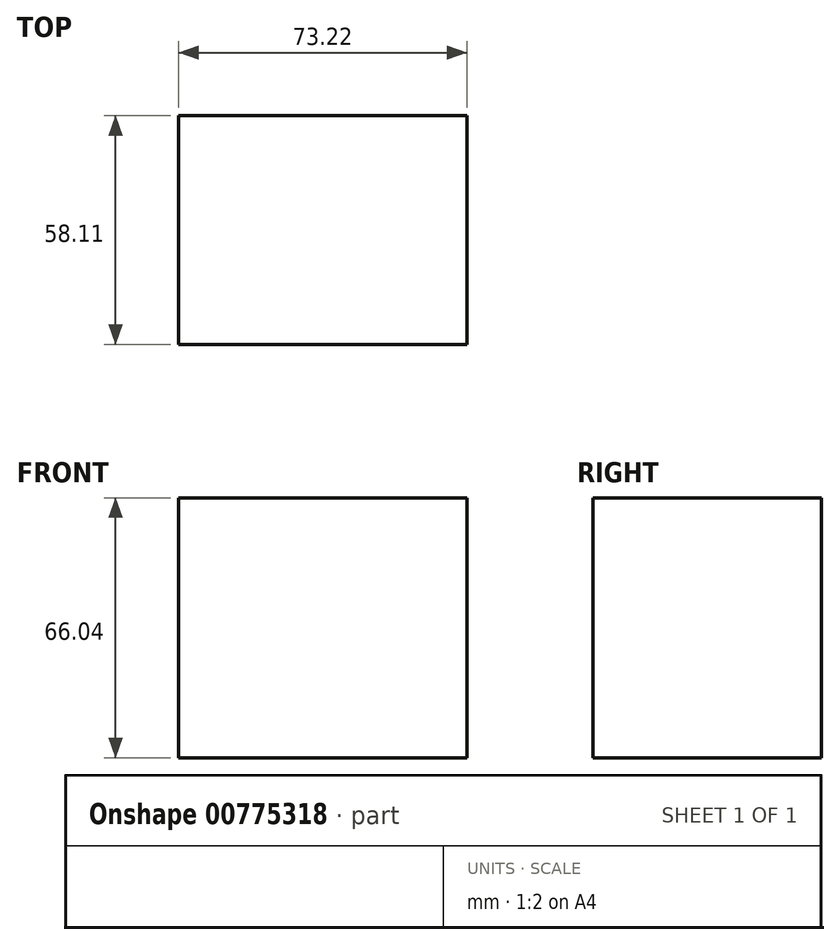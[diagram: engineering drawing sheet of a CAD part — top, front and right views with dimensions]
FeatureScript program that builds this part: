
annotation { "Feature Type Name" : "Feature", "Feature Type Description" : "" }
export const myFeature = defineFeature(function(context is Context, id is Id, definition is map)
    precondition{}
    {
        {
            var Q0;
            Q0=qCreatedBy(makeId("Top.planeOp"),FACE);
            var sketch = newSketch(context, id + "F0", { "sketchPlane" : qUnion([Q0])});
            skLineSegment(sketch, "E0.bottom", {"start": v(-40.55, 22.37) * mm, "end": v(32.67, 22.37) * mm});
            skLineSegment(sketch, "E0.top", {"start": v(-40.55, -35.74) * mm, "end": v(32.67, -35.74) * mm});
            skLineSegment(sketch, "E0.left", {"start": v(-40.55, 22.37) * mm, "end": v(-40.55, -35.74) * mm});
            skLineSegment(sketch, "E0.right", {"start": v(32.67, 22.37) * mm, "end": v(32.67, -35.74) * mm});
            skSolve(sketch);
        }
        {
            var Q0;
            Q0 = qSketchRegion(id + "F0", true);
            extrude(context, id + "F1", {"entities" : qUnion([Q0]), "depth" : 66.04 * mm, "offsetDistance" : 25.4 * mm});
        }
    });
